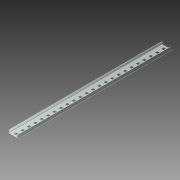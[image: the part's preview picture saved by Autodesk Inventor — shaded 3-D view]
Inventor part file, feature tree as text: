
AUTODESK INVENTOR PART (.ipt)
format: ipt  version: 2013 (Build 170138000, 138)  size: 357,376 bytes
history: native  units: in
note: dims shown in document units (in); Inventor stores cm internally (conversion verified against a paired STEP export)
features: other x28, extrude x24, sheet_metal_op x4, sketch x4, pattern_linear x2
ambient origin geometry x8: Origin, YZ Plane, XZ Plane, XY Plane, X Axis, Y Axis, Z Axis, Center Point
bodies: Solid1 (feature_tree)
feature tree (62):
  sheet_metal_op  "Face1"
  sheet_metal_op  "Flange1"
  other  "Corner Chamfer1"
  pattern_linear  "Rectangular Pattern1"  Spacing1=0.0235in  [1 undecoded]
  pattern_linear  "Rectangular Pattern2"  Spacing1=0.094in  [1 undecoded]
  sketch  "Sketch1"  dims[d0=0.867in]
  other  "Plate1"
  sketch  "Sketch2"  dims[d1=12.0in]
  other  "Plate2"
  sheet_metal_op  "Bend1"
  sheet_metal_op  "Corner1"
  sketch  "Sketch4"  dims[d2=0.03in]
  sketch  "Sketch5"  dims[d3=0.047in d4=0.0235in d5=0.094in d6=0.03in d7=0.222in d8=105.0deg d9=0.03in d10=0.188in d11=0.047in d12=0.03in d13=0.075in d14=0.25in d15=45.0deg d16=0.182in d17=0.047in d18=0.0in d19=0.02in d20=13.7795in d22=0.5in d23=0.179in d24=1.0in d25=0.0in d26=0.0in d27=0.0in d28=9.4488in d30=0.5in d31=0.0in d32=0.0in d33=0.0in d34=0.0in d35=0.0in d36=0.0in d37=0.0in d38=0.0in d39=0.0in d40=0.0in d41=0.0in d42=0.0in d43=0.0in d44=0.0in d45=0.0in d46=0.0in d47=0.0in d48=0.0in d49=0.0in d50=0.0in d51=0.0in d52=0.0in d53=0.0in d54=0.0in d55=0.0in d56=0.0in d57=0.0in d58=0.0in d59=0.0in d60=0.0in d61=0.0in d62=0.0in d63=0.0in d64=0.0in d65=0.0in d66=0.0in d67=0.0in d68=0.0in d69=0.0in d70=0.0in d71=0.0in d72=0.0in d73=0.0in d74=0.0in d75=0.0in d76=0.0in]
  other  "Srf1"
  other  "Srf2"
  other  "Srf3"
  other  "Srf4"
  other  "Srf5"
  other  "Srf6"
  other  "Srf7"
  other  "Srf8"
  other  "Srf9"
  other  "Srf10"
  other  "Srf11"
  other  "Srf12"
  other  "Srf13"
  other  "Srf14"
  other  "Srf15"
  other  "Srf16"
  other  "Srf17"
  other  "Srf18"
  other  "Srf19"
  other  "Srf20"
  other  "Srf21"
  other  "Srf22"
  other  "Srf23"
  other  "Srf24"
  other  "Cut1"
  extrude  "ExtrusionSrf1"  Depth=0.03in
  extrude  "ExtrusionSrf2"  Depth=0.222in TaperAngle=105.0deg
  extrude  "ExtrusionSrf3"  Depth=0.188in
  extrude  "ExtrusionSrf4"  Depth=0.047in
  extrude  "ExtrusionSrf5"  Depth=0.03in
  extrude  "ExtrusionSrf6"  Depth=0.075in TaperAngle=45.0deg
  extrude  "ExtrusionSrf7"  Depth=0.182in
  extrude  "ExtrusionSrf8"  Depth=0.047in
  extrude  "ExtrusionSrf9"  TaperAngle=0.0deg  [1 undecoded]
  extrude  "ExtrusionSrf10"  Depth=0.02in
  extrude  "ExtrusionSrf11"  Depth=13.7795in
  extrude  "ExtrusionSrf12"  Depth=0.179in
  extrude  "ExtrusionSrf13"  Depth=1.0in TaperAngle=0.0deg
  extrude  "ExtrusionSrf14"  Depth=9.4488in TaperAngle=0.0deg
  extrude  "ExtrusionSrf15"  [1 undecoded]
  extrude  "ExtrusionSrf16"  [1 undecoded]
  extrude  "ExtrusionSrf17"  [1 undecoded]
  extrude  "ExtrusionSrf18"  [1 undecoded]
  extrude  "ExtrusionSrf19"  [1 undecoded]
  extrude  "ExtrusionSrf20"  [1 undecoded]
  extrude  "ExtrusionSrf21"  [1 undecoded]
  extrude  "ExtrusionSrf22"  [1 undecoded]
  extrude  "ExtrusionSrf23"  [1 undecoded]
  extrude  "ExtrusionSrf24"  [1 undecoded]
note: 13 required parameter values undecoded (feature->parameter linkage not recoverable at this tier; creation-order binding heuristic only, values carry confidence <= 0.55)
